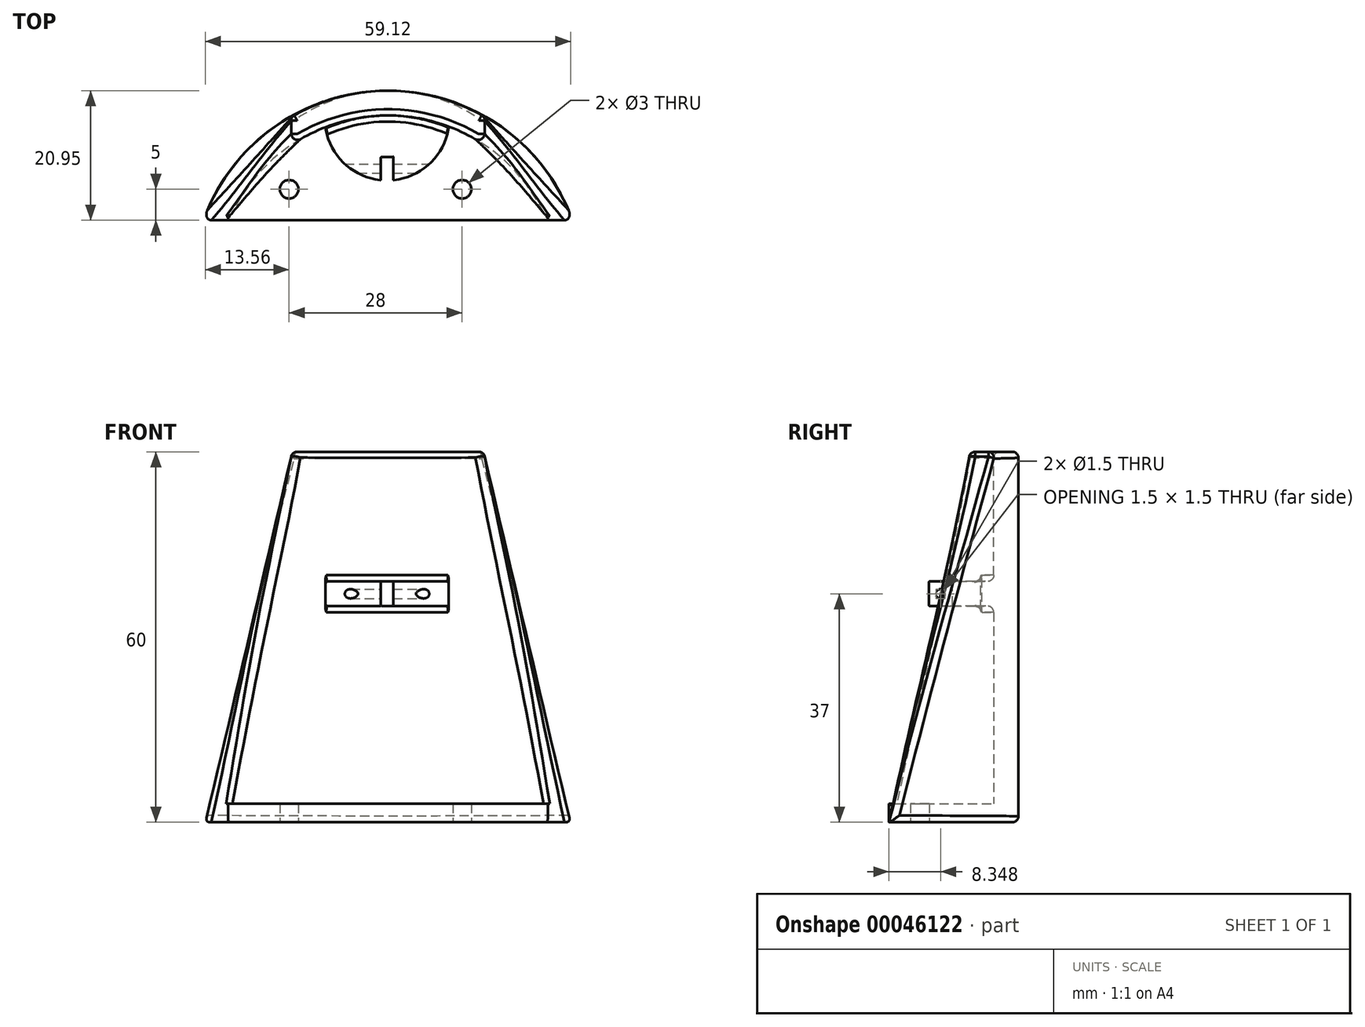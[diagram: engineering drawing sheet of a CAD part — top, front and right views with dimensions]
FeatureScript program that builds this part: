
annotation { "Feature Type Name" : "Feature", "Feature Type Description" : "" }
export const myFeature = defineFeature(function(context is Context, id is Id, definition is map)
    precondition{}
    {
        {
            var Q0;
            Q0=qCreatedBy(makeId("Top.planeOp"),FACE);
            var sketch = newSketch(context, id + "F0", { "sketchPlane" : qUnion([Q0])});
            skLineSegment(sketch, "E0.bottom", {"start": v(-24.17, 9.79) * mm, "end": v(35.83, 9.79) * mm, "construction": true});
            skLineSegment(sketch, "E0.top", {"start": v(-24.17, -15.21) * mm, "end": v(-20.17, -15.21) * mm});
            skLineSegment(sketch, "E0.left", {"start": v(-24.17, 9.79) * mm, "end": v(-24.17, -15.21) * mm, "construction": true});
            skLineSegment(sketch, "E0.right", {"start": v(35.83, 9.79) * mm, "end": v(35.83, -15.21) * mm, "construction": true});
            skArc(sketch, "E1", {"start": v(35.83, -15.21) * mm, "mid": v(5.83, 5.74) * mm, "end": v(-24.17, -15.21) * mm});
            skArc(sketch, "E2", {"start": v(31.83, -15.21) * mm, "mid": v(5.83, 1.74) * mm, "end": v(-20.17, -15.21) * mm});
            skLineSegment(sketch, "E3.trimOffspring", {"start": v(31.83, -15.21) * mm, "end": v(35.83, -15.21) * mm});
            skLineSegment(sketch, "E4", {"start": v(-20.17, -15.21) * mm, "end": v(31.83, -15.21) * mm});
            skCircle(sketch, "E5", {"center": v(-10.17, -10.21) * mm, "radius": 1.5 * mm});
            skCircle(sketch, "E6", {"center": v(17.83, -10.21) * mm, "radius": 1.5 * mm});
            skSolve(sketch);
        }
        {
            var Q0;
            Q0=qCreatedBy(makeId("Top.planeOp"),FACE);
            cPlane(context, id + "F1", {"entities" : qUnion([Q0]), "cplaneType" : CPlaneType.OFFSET, "offset" : 60 * mm, "width" : 150 * mm, "height" : 150 * mm});
        }
        {
            var Q0;
            Q0=qCreatedBy(id+"F1.planeOp",FACE);
            var sketch = newSketch(context, id + "F2", { "sketchPlane" : qUnion([Q0])});
            skArc(sketch, "E7", {"start": v(21.31, -2.84) * mm, "mid": v(5.83, 1.74) * mm, "end": v(-9.65, -2.84) * mm});
            skArc(sketch, "E8", {"start": v(21.31, 1.74) * mm, "mid": v(5.83, 5.74) * mm, "end": v(-9.65, 1.74) * mm});
            skPoint(sketch, "E8.startSnap0", {"position": v(5.83, 1.74) * mm});
            skPoint(sketch, "E8.endSnap0", {"position": v(5.83, 1.74) * mm});
            skLineSegment(sketch, "E9", {"start": v(-9.65, 1.74) * mm, "end": v(-9.65, -2.84) * mm});
            skLineSegment(sketch, "E10", {"start": v(21.31, 1.74) * mm, "end": v(21.31, -2.84) * mm});
            skSolve(sketch);
        }
        {
            var Q0;
            Q0=makeQuery(id+"F0.imprint","IMPRINT",FACE,{"disambiguationData":[TD([[makeQuery(id+"F0.imprint","IMPRINT",EDGE,{"derivedFrom":sQuery(id+"F0.wireOp",EDGE,"E0.top")}),1.0]])]});
            var Q1;
            Q1=makeQuery(id+"F2.imprint","IMPRINT",FACE,{"disambiguationData":[TD([[makeQuery(id+"F2.imprint","IMPRINT",EDGE,{"derivedFrom":sQuery(id+"F2.wireOp",EDGE,"E7")}),-1.0]])]});
            loft(context, id + "F3", {"sheetProfilesArray" : [{ "sheetProfileEntities" : qUnion([Q0]) }, { "sheetProfileEntities" : qUnion([Q1]) }]});
        }
        {
            var Q0;
            Q0=makeQuery(id+"F0.imprint","IMPRINT",FACE,{"disambiguationData":[TD([[makeQuery(id+"F0.imprint","IMPRINT",EDGE,{"derivedFrom":sQuery(id+"F0.wireOp",EDGE,"E2")}),1.0]])]});
            extrude(context, id + "F4", {"entities" : qUnion([Q0]), "operationType" : NewBodyOperationType.ADD, "depth" : 3 * mm});
        }
        {
            var Q0;
            Q0=makeQuery(id+"F4.opExtrude","SWEPT_EDGE",EDGE,{"disambiguationData":[OSD([sQuery(id+"F0.wireOp",EDGE,"E0.top"),sQuery(id+"F0.wireOp",EDGE,"E2"),sQuery(id+"F0.wireOp",EDGE,"E4")])]});
            var Q1;
            Q1=makeQuery(id+"F4.opExtrude","SWEPT_EDGE",EDGE,{"disambiguationData":[OSD([sQuery(id+"F0.wireOp",EDGE,"E2"),sQuery(id+"F0.wireOp",EDGE,"E3.trimOffspring"),sQuery(id+"F0.wireOp",EDGE,"E4")])]});
            var Q2;
            {var subQ0=sQuery(id+"F0.wireOp",EDGE,"E2");var subQ1=sQuery(id+"F0.wireOp",EDGE,"E4");Q2=makeQuery(id+"F4.boolean.opBoolean","SPLIT",EDGE,{"disambiguationData":[TD([makeQuery(id+"F3.opLoft","SWEPT_FACE",FACE,{"disambiguationData":[OSD([sQuery(id+"F0.wireOp",EDGE,"E1"),subQ0,sQuery(id+"F0.wireOp",EDGE,"E3.trimOffspring"),subQ1,sQuery(id+"F2.wireOp",EDGE,"E7"),sQuery(id+"F2.wireOp",EDGE,"E8"),sQuery(id+"F2.wireOp",EDGE,"E10")])]})])],"derivedFrom":makeQuery(id+"F4.opExtrude","CAP_EDGE",EDGE,{"disambiguationData":[OSD([subQ0])],"isStart":false})});}
            var Q3;
            {var subQ0=sQuery(id+"F0.wireOp",EDGE,"E2");var subQ1=sQuery(id+"F0.wireOp",EDGE,"E4");Q3=makeQuery(id+"F4.boolean.opBoolean","SPLIT",EDGE,{"disambiguationData":[TD([makeQuery(id+"F3.opLoft","SWEPT_FACE",FACE,{"disambiguationData":[OSD([sQuery(id+"F0.wireOp",EDGE,"E0.top"),sQuery(id+"F0.wireOp",EDGE,"E1"),subQ0,subQ1,sQuery(id+"F2.wireOp",EDGE,"E7"),sQuery(id+"F2.wireOp",EDGE,"E8"),sQuery(id+"F2.wireOp",EDGE,"E9")])]})])],"derivedFrom":makeQuery(id+"F4.opExtrude","CAP_EDGE",EDGE,{"disambiguationData":[OSD([subQ0])],"isStart":false})});}
            fillet(context, id + "F5", {"entities" : qUnion([Q0, Q1, Q2, Q3]), "radius" : .2 * mm, "tangentPropagation" : true, "allowEdgeOverflow" : false});
        }
        {
            var Q0;
            Q0=makeQuery(id+"F3.opLoft","SWEPT_EDGE",EDGE,{"disambiguationData":[OSD([sQuery(id+"F0.wireOp",EDGE,"E1"),sQuery(id+"F0.wireOp",EDGE,"E3.trimOffspring"),sQuery(id+"F2.wireOp",EDGE,"E8"),sQuery(id+"F2.wireOp",EDGE,"E10")])]});
            var Q1;
            Q1=makeQuery(id+"F3.opLoft","SWEPT_EDGE",EDGE,{"disambiguationData":[OSD([sQuery(id+"F0.wireOp",EDGE,"E2"),sQuery(id+"F0.wireOp",EDGE,"E3.trimOffspring"),sQuery(id+"F0.wireOp",EDGE,"E4"),sQuery(id+"F2.wireOp",EDGE,"E7"),sQuery(id+"F2.wireOp",EDGE,"E10")])]});
            var Q2;
            Q2=makeQuery(id+"F3.opLoft","MID_CAP_EDGE",EDGE,{"disambiguationData":[OSD([sQuery(id+"F2.wireOp",EDGE,"E7"),sQuery(id+"F2.wireOp",EDGE,"E8"),sQuery(id+"F2.wireOp",EDGE,"E10")])],"capPos":1.0});
            var Q3;
            Q3=makeQuery(id+"F3.opLoft","MID_CAP_EDGE",EDGE,{"disambiguationData":[OSD([sQuery(id+"F2.wireOp",EDGE,"E7"),sQuery(id+"F2.wireOp",EDGE,"E9"),sQuery(id+"F2.wireOp",EDGE,"E10")])],"capPos":1.0});
            var Q4;
            Q4=makeQuery(id+"F3.opLoft","MID_CAP_EDGE",EDGE,{"disambiguationData":[OSD([sQuery(id+"F2.wireOp",EDGE,"E8"),sQuery(id+"F2.wireOp",EDGE,"E9"),sQuery(id+"F2.wireOp",EDGE,"E10")])],"capPos":1.0});
            var Q5;
            Q5=makeQuery(id+"F3.opLoft","SWEPT_EDGE",EDGE,{"disambiguationData":[OSD([sQuery(id+"F0.wireOp",EDGE,"E0.top"),sQuery(id+"F0.wireOp",EDGE,"E2"),sQuery(id+"F0.wireOp",EDGE,"E4"),sQuery(id+"F2.wireOp",EDGE,"E7"),sQuery(id+"F2.wireOp",EDGE,"E9")])]});
            var Q6;
            Q6=makeQuery(id+"F3.opLoft","MID_CAP_EDGE",EDGE,{"disambiguationData":[OSD([sQuery(id+"F2.wireOp",EDGE,"E7"),sQuery(id+"F2.wireOp",EDGE,"E8"),sQuery(id+"F2.wireOp",EDGE,"E9")])],"capPos":1.0});
            var Q7;
            Q7=makeQuery(id+"F3.opLoft","SWEPT_EDGE",EDGE,{"disambiguationData":[OSD([sQuery(id+"F0.wireOp",EDGE,"E0.top"),sQuery(id+"F0.wireOp",EDGE,"E1"),sQuery(id+"F2.wireOp",EDGE,"E8"),sQuery(id+"F2.wireOp",EDGE,"E9")])]});
            var Q8;
            Q8=makeQuery(id+"F3.opLoft","MID_CAP_EDGE",EDGE,{"disambiguationData":[OSD([sQuery(id+"F0.wireOp",EDGE,"E0.top"),sQuery(id+"F0.wireOp",EDGE,"E1"),sQuery(id+"F0.wireOp",EDGE,"E3.trimOffspring")])],"capPos":0.0});
            fillet(context, id + "F6", {"entities" : qUnion([Q0, Q1, Q2, Q3, Q4, Q5, Q6, Q7, Q8]), "radius" : 1 * mm, "tangentPropagation" : true, "allowEdgeOverflow" : false});
        }
        {
            var Q0;
            Q0=qCreatedBy(makeId("Top.planeOp"),FACE);
            cPlane(context, id + "F7", {"entities" : qUnion([Q0]), "cplaneType" : CPlaneType.OFFSET, "offset" : 35 * mm, "width" : 150 * mm, "height" : 150 * mm});
        }
        {
            var Q0;
            Q0=qCreatedBy(id+"F7.planeOp",FACE);
            var sketch = newSketch(context, id + "F8", { "sketchPlane" : qUnion([Q0])});
            skArc(sketch, "E11", {"start": v(-4.32, 0) * mm, "mid": v(5.68, -8.79) * mm, "end": v(15.68, 0) * mm});
            skLineSegment(sketch, "E12.bottom", {"start": v(-4.32, 0) * mm, "end": v(15.68, 0) * mm});
            skLineSegment(sketch, "E13.top", {"start": v(-4.32, 3) * mm, "end": v(15.68, 3) * mm});
            skLineSegment(sketch, "E13.left", {"start": v(-4.32, 0) * mm, "end": v(-4.32, 3) * mm});
            skLineSegment(sketch, "E13.right", {"start": v(15.68, 0) * mm, "end": v(15.68, 3) * mm});
            skLineSegment(sketch, "E14.top", {"start": v(4.68, -5) * mm, "end": v(6.68, -5) * mm});
            skLineSegment(sketch, "E14.left", {"start": v(4.68, -8.74) * mm, "end": v(4.68, -5) * mm});
            skLineSegment(sketch, "E14.right", {"start": v(6.68, -8.74) * mm, "end": v(6.68, -5) * mm});
            skLineSegment(sketch, "E15", {"start": v(5.68, 3) * mm, "end": v(5.68, -5) * mm, "construction": true});
            skPoint(sketch, "E16.orphan", {"position": v(5.68, -8.74) * mm});
            skSolve(sketch);
        }
        {
            var Q0;
            Q0=makeQuery(id+"F8.imprint","IMPRINT",FACE,{"disambiguationData":[TD([[makeQuery(id+"F8.imprint","IMPRINT",EDGE,{"derivedFrom":sQuery(id+"F8.wireOp",EDGE,"E12.bottom")}),1.0]])]});
            var Q1;
            {var subQ0=sQuery(id+"F8.wireOp",EDGE,"E12.bottom");Q1=makeQuery(id+"F8.imprint","IMPRINT",FACE,{"disambiguationData":[TD([[makeQuery(id+"F8.imprint","IMPRINT",EDGE,{"derivedFrom":subQ0}),-1.0]])]});}
            extrude(context, id + "F9", {"entities" : qUnion([Q0, Q1]), "operationType" : NewBodyOperationType.ADD, "depth" : 4 * mm});
        }
        {
            var Q0;
            Q0=makeQuery(id+"F9.boolean.opBoolean","INTERSECT",EDGE,{"derivedFrom":[makeQuery(id+"F3.opLoft","SWEPT_FACE",FACE,{"disambiguationData":[OSD([sQuery(id+"F0.wireOp",EDGE,"E0.top"),sQuery(id+"F0.wireOp",EDGE,"E2"),sQuery(id+"F0.wireOp",EDGE,"E3.trimOffspring"),sQuery(id+"F0.wireOp",EDGE,"E4"),sQuery(id+"F2.wireOp",EDGE,"E7"),sQuery(id+"F2.wireOp",EDGE,"E9"),sQuery(id+"F2.wireOp",EDGE,"E10")])]}),makeQuery(id+"F9.opExtrude","CAP_FACE",FACE,{"disambiguationData":[OSD([sQuery(id+"F8.wireOp",EDGE,"E11"),sQuery(id+"F8.wireOp",EDGE,"E13.top"),sQuery(id+"F8.wireOp",EDGE,"E13.left"),sQuery(id+"F8.wireOp",EDGE,"E13.right"),sQuery(id+"F8.wireOp",EDGE,"E14.top"),sQuery(id+"F8.wireOp",EDGE,"E14.left"),sQuery(id+"F8.wireOp",EDGE,"E14.right")])],"isStart":false})]});
            var Q1;
            Q1=makeQuery(id+"F9.boolean.opBoolean","INTERSECT",EDGE,{"derivedFrom":[makeQuery(id+"F3.opLoft","SWEPT_FACE",FACE,{"disambiguationData":[OSD([sQuery(id+"F0.wireOp",EDGE,"E0.top"),sQuery(id+"F0.wireOp",EDGE,"E2"),sQuery(id+"F0.wireOp",EDGE,"E3.trimOffspring"),sQuery(id+"F0.wireOp",EDGE,"E4"),sQuery(id+"F2.wireOp",EDGE,"E7"),sQuery(id+"F2.wireOp",EDGE,"E9"),sQuery(id+"F2.wireOp",EDGE,"E10")])]}),makeQuery(id+"F9.opExtrude","SWEPT_FACE",FACE,{"disambiguationData":[OSD([sQuery(id+"F8.wireOp",EDGE,"E13.left")])]})]});
            var Q2;
            Q2=makeQuery(id+"F9.boolean.opBoolean","INTERSECT",EDGE,{"derivedFrom":[makeQuery(id+"F3.opLoft","SWEPT_FACE",FACE,{"disambiguationData":[OSD([sQuery(id+"F0.wireOp",EDGE,"E0.top"),sQuery(id+"F0.wireOp",EDGE,"E2"),sQuery(id+"F0.wireOp",EDGE,"E3.trimOffspring"),sQuery(id+"F0.wireOp",EDGE,"E4"),sQuery(id+"F2.wireOp",EDGE,"E7"),sQuery(id+"F2.wireOp",EDGE,"E9"),sQuery(id+"F2.wireOp",EDGE,"E10")])]}),makeQuery(id+"F9.opExtrude","CAP_FACE",FACE,{"disambiguationData":[OSD([sQuery(id+"F8.wireOp",EDGE,"E11"),sQuery(id+"F8.wireOp",EDGE,"E13.top"),sQuery(id+"F8.wireOp",EDGE,"E13.left"),sQuery(id+"F8.wireOp",EDGE,"E13.right"),sQuery(id+"F8.wireOp",EDGE,"E14.top"),sQuery(id+"F8.wireOp",EDGE,"E14.left"),sQuery(id+"F8.wireOp",EDGE,"E14.right")])],"isStart":true})]});
            var Q3;
            Q3=makeQuery(id+"F9.boolean.opBoolean","INTERSECT",EDGE,{"derivedFrom":[makeQuery(id+"F3.opLoft","SWEPT_FACE",FACE,{"disambiguationData":[OSD([sQuery(id+"F0.wireOp",EDGE,"E0.top"),sQuery(id+"F0.wireOp",EDGE,"E2"),sQuery(id+"F0.wireOp",EDGE,"E3.trimOffspring"),sQuery(id+"F0.wireOp",EDGE,"E4"),sQuery(id+"F2.wireOp",EDGE,"E7"),sQuery(id+"F2.wireOp",EDGE,"E9"),sQuery(id+"F2.wireOp",EDGE,"E10")])]}),makeQuery(id+"F9.opExtrude","SWEPT_FACE",FACE,{"disambiguationData":[OSD([sQuery(id+"F8.wireOp",EDGE,"E13.right")])]})]});
            fillet(context, id + "F10", {"entities" : qUnion([Q0, Q1, Q2, Q3]), "radius" : 1 * mm, "tangentPropagation" : true, "allowEdgeOverflow" : false});
        }
        {
            var Q0;
            {var subQ0=sQuery(id+"F8.wireOp",EDGE,"E11");Q0=makeQuery(id+"F9.opExtrude","CAP_EDGE",EDGE,{"disambiguationData":[OSD([subQ0]),TDD([makeQuery(id+"F8.imprint","IMPRINT",EDGE,{"disambiguationData":[TD([[makeQuery(id+"F8.imprint","INTERSECT",VERTEX,{"derivedFrom":[subQ0,sQuery(id+"F8.wireOp",EDGE,"E14.right")]}),-1.0]])],"derivedFrom":subQ0})])],"isStart":false});}
            var Q1;
            Q1=makeQuery(id+"F9.opExtrude","CAP_EDGE",EDGE,{"disambiguationData":[OSD([sQuery(id+"F8.wireOp",EDGE,"E14.top")])],"isStart":false});
            var Q2;
            Q2=makeQuery(id+"F9.opExtrude","CAP_EDGE",EDGE,{"disambiguationData":[OSD([sQuery(id+"F8.wireOp",EDGE,"E14.right")])],"isStart":false});
            var Q3;
            Q3=makeQuery(id+"F9.opExtrude","CAP_EDGE",EDGE,{"disambiguationData":[OSD([sQuery(id+"F8.wireOp",EDGE,"E14.left")])],"isStart":false});
            var Q4;
            Q4=makeQuery(id+"F9.opExtrude","SWEPT_EDGE",EDGE,{"disambiguationData":[OSD([sQuery(id+"F8.wireOp",EDGE,"E11"),sQuery(id+"F8.wireOp",EDGE,"E14.left")])]});
            var Q5;
            Q5=makeQuery(id+"F9.opExtrude","SWEPT_EDGE",EDGE,{"disambiguationData":[OSD([sQuery(id+"F8.wireOp",EDGE,"E11"),sQuery(id+"F8.wireOp",EDGE,"E14.right")])]});
            var Q6;
            Q6=makeQuery(id+"F9.opExtrude","SWEPT_EDGE",EDGE,{"disambiguationData":[OSD([sQuery(id+"F8.wireOp",EDGE,"E14.top"),sQuery(id+"F8.wireOp",EDGE,"E14.left")])]});
            var Q7;
            Q7=makeQuery(id+"F9.opExtrude","CAP_EDGE",EDGE,{"disambiguationData":[OSD([sQuery(id+"F8.wireOp",EDGE,"E14.top")])],"isStart":true});
            var Q8;
            Q8=makeQuery(id+"F9.opExtrude","CAP_EDGE",EDGE,{"disambiguationData":[OSD([sQuery(id+"F8.wireOp",EDGE,"E14.right")])],"isStart":true});
            var Q9;
            {var subQ0=sQuery(id+"F8.wireOp",EDGE,"E11");Q9=makeQuery(id+"F9.opExtrude","CAP_EDGE",EDGE,{"disambiguationData":[OSD([subQ0]),TDD([makeQuery(id+"F8.imprint","IMPRINT",EDGE,{"disambiguationData":[TD([[makeQuery(id+"F8.imprint","INTERSECT",VERTEX,{"derivedFrom":[subQ0,sQuery(id+"F8.wireOp",EDGE,"E14.right")]}),-1.0]])],"derivedFrom":subQ0})])],"isStart":true});}
            var Q10;
            {var subQ0=sQuery(id+"F8.wireOp",EDGE,"E11");Q10=makeQuery(id+"F9.opExtrude","CAP_EDGE",EDGE,{"disambiguationData":[OSD([subQ0]),TDD([makeQuery(id+"F8.imprint","IMPRINT",EDGE,{"disambiguationData":[TD([[makeQuery(id+"F8.imprint","INTERSECT",VERTEX,{"derivedFrom":[subQ0,sQuery(id+"F8.wireOp",EDGE,"E14.left")]}),1.0]])],"derivedFrom":subQ0})])],"isStart":true});}
            var Q11;
            {var subQ0=sQuery(id+"F8.wireOp",EDGE,"E11");Q11=makeQuery(id+"F9.opExtrude","CAP_EDGE",EDGE,{"disambiguationData":[OSD([subQ0]),TDD([makeQuery(id+"F8.imprint","IMPRINT",EDGE,{"disambiguationData":[TD([[makeQuery(id+"F8.imprint","INTERSECT",VERTEX,{"derivedFrom":[subQ0,sQuery(id+"F8.wireOp",EDGE,"E14.left")]}),1.0]])],"derivedFrom":subQ0})])],"isStart":false});}
            fillet(context, id + "F11", {"entities" : qUnion([Q0, Q1, Q2, Q3, Q4, Q5, Q6, Q7, Q8, Q9, Q10, Q11]), "radius" : .1 * mm, "tangentPropagation" : true, "allowEdgeOverflow" : false});
        }
        {
            var Q0;
            Q0=makeQuery(id+"F9.opExtrude","SWEPT_FACE",FACE,{"disambiguationData":[OSD([sQuery(id+"F8.wireOp",EDGE,"E14.left")])]});
            var sketch = newSketch(context, id + "F12", { "sketchPlane" : qUnion([Q0])});
            skCircle(sketch, "E17", {"center": v(-6.86, 37) * mm, "radius": 0.75 * mm});
            skPoint(sketch, "E17.centerSnap0", {"position": v(-6.86, 38.9) * mm});
            skPoint(sketch, "E17.centerSnap1", {"position": v(-8.62, 37) * mm});
            skSolve(sketch);
        }
        {
            var Q0;
            Q0=makeQuery(id+"F12.imprint","IMPRINT",FACE,{"disambiguationData":[TD([[makeQuery(id+"F12.imprint","IMPRINT",EDGE,{"derivedFrom":sQuery(id+"F12.wireOp",EDGE,"E17")}),1.0]])]});
            var Q1;
            {var subQ0=sQuery(id+"F8.wireOp",EDGE,"E11");Q1=makeQuery(id+"F9.opExtrude","SWEPT_FACE",FACE,{"disambiguationData":[OSD([subQ0]),TDD([makeQuery(id+"F8.imprint","IMPRINT",EDGE,{"disambiguationData":[TD([[makeQuery(id+"F8.imprint","INTERSECT",VERTEX,{"derivedFrom":[subQ0,sQuery(id+"F8.wireOp",EDGE,"E14.left")]}),1.0]])],"derivedFrom":subQ0})])]});}
            var Q2;
            {var subQ0=sQuery(id+"F8.wireOp",EDGE,"E11");Q2=makeQuery(id+"F9.opExtrude","SWEPT_FACE",FACE,{"disambiguationData":[OSD([subQ0]),TDD([makeQuery(id+"F8.imprint","IMPRINT",EDGE,{"disambiguationData":[TD([[makeQuery(id+"F8.imprint","INTERSECT",VERTEX,{"derivedFrom":[subQ0,sQuery(id+"F8.wireOp",EDGE,"E14.right")]}),-1.0]])],"derivedFrom":subQ0})])]});}
            extrude(context, id + "F13", {"entities" : qUnion([Q0]), "operationType" : NewBodyOperationType.REMOVE, "endBound" : BoundingType.UP_TO_SURFACE, "oppositeDirection" : true, "endBoundEntityFace" : qUnion([Q1]), "depth" : 25 * mm, "hasSecondDirection" : true, "secondDirectionBound" : SecondDirectionBoundingType.UP_TO_SURFACE, "secondDirectionOppositeDirection" : false, "secondDirectionBoundEntityFace" : qUnion([Q2]), "secondDirectionDepth" : 25 * mm});
        }
    });
